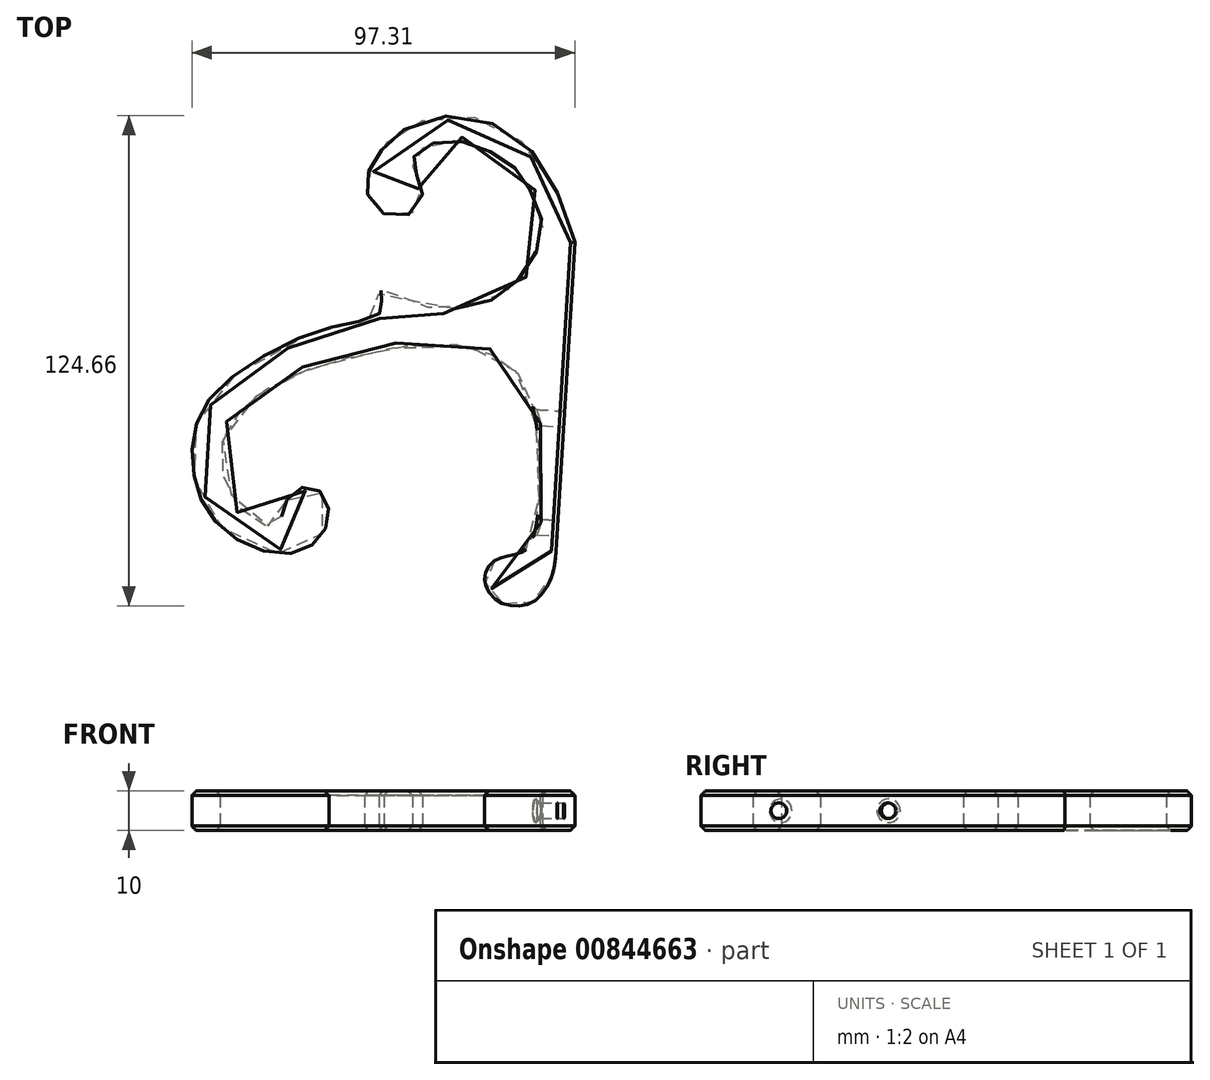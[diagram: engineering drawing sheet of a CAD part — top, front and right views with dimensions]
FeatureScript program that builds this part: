
annotation { "Feature Type Name" : "Feature", "Feature Type Description" : "" }
export const myFeature = defineFeature(function(context is Context, id is Id, definition is map)
    precondition{}
    {
        {
            var Q0;
            Q0=qCreatedBy(makeId("Top.planeOp"),FACE);
            var sketch = newSketch(context, id + "F0", { "sketchPlane" : qUnion([Q0])});
            skLineSegment(sketch, "E0", {"start": v(42, -44.18) * mm, "end": v(46.84, 34.44) * mm});
            skFitSpline(sketch, "E1", {"points": [v(46.84, 34.44) * mm, v(36.12, 57.16) * mm, v(16.47, 66.6) * mm, v(0.13, 60.73) * mm, v(-3.7, 55.37) * mm, v(-6.55, 49.76) * mm, v(-4.57, 44.53) * mm, v(0.03, 40.92) * mm, v(6.44, 42.64) * mm, v(8.06, 48.05) * mm, v(6.35, 52.02) * mm, v(5.63, 55.27) * mm, v(8.53, 58.54) * mm, v(16.08, 60.18) * mm, v(24.29, 57.88) * mm, v(31.84, 52.96) * mm, v(35.78, 47.05) * mm, v(38.57, 37.67) * mm, v(34.06, 26.93) * mm, v(26.02, 19.8) * mm, v(12.85, 17.45) * mm, v(3.55, 19.9) * mm, v(-0.96, 22.42) * mm, v(-2.23, 22.33) * mm, v(-2.95, 20.97) * mm, v(-1.68, 17.82) * mm, v(-5.79, 14.9) * mm, v(-18.56, 11.77) * mm, v(-40.39, 0) * mm, v(-49.26, -11.44) * mm, v(-50.24, -22.89) * mm, v(-46.9, -33.18) * mm, v(-37.7, -41.93) * mm, v(-25.15, -44.64) * mm, v(-17.84, -40.4) * mm, v(-15.67, -33.8) * mm, v(-18.56, -28.4) * mm, v(-24.07, -28.57) * mm, v(-27.4, -33.8) * mm, v(-28.58, -36.97) * mm, v(-34, -36.97) * mm, v(-40.7, -29.44) * mm, v(-43.14, -18.28) * mm, v(-38.31, -8.62) * mm, v(-30.17, -2.13) * mm, v(-15.4, 3.8) * mm, v(12.89, 8.63) * mm, v(26.1, 5.7) * mm, v(33.15, 0) * mm, v(37.09, -12.37) * mm, v(37.75, -31.08) * mm, v(35.32, -42.56) * mm, v(31.9, -44.82) * mm, v(25.93, -46.9) * mm, v(23.95, -51.95) * mm, v(28.19, -57.27) * mm, v(36.5, -56.82) * mm, v(41.1, -50.05) * mm, v(42, -44.18) * mm], "startDerivative": vector(-287.05, 889.88) * mm, "endDerivative": vector(28.23, 413.52) * mm});
            skSolve(sketch);
        }
        {
            var Q0;
            Q0=makeQuery(id+"F0.imprint","IMPRINT",FACE,{"disambiguationData":[TD([[makeQuery(id+"F0.imprint","IMPRINT",EDGE,{"derivedFrom":sQuery(id+"F0.wireOp",EDGE,"E0")}),1.0]])]});
            extrude(context, id + "F1", {"entities" : qUnion([Q0]), "depth" : 10 * mm, "offsetDistance" : 25 * mm});
        }
        {
            var Q0;
            Q0=makeQuery(id+"F1.opExtrude","CAP_EDGE",EDGE,{"disambiguationData":[OSD([sQuery(id+"F0.wireOp",EDGE,"E1")])],"isStart":false});
            var Q1;
            Q1=makeQuery(id+"F1.opExtrude","CAP_EDGE",EDGE,{"disambiguationData":[OSD([sQuery(id+"F0.wireOp",EDGE,"E0")])],"isStart":false});
            var Q2;
            Q2=makeQuery(id+"F1.opExtrude","CAP_EDGE",EDGE,{"disambiguationData":[OSD([sQuery(id+"F0.wireOp",EDGE,"E1")])],"isStart":true});
            var Q3;
            Q3=makeQuery(id+"F1.opExtrude","CAP_EDGE",EDGE,{"disambiguationData":[OSD([sQuery(id+"F0.wireOp",EDGE,"E0")])],"isStart":true});
            chamfer(context, id + "F2", {"entities" : qUnion([Q0, Q1, Q2, Q3]), "width" : 1.1 * mm, "tangentPropagation" : true});
        }
        {
            var Q0;
            Q0=makeQuery(id+"F1.opExtrude","SWEPT_FACE",FACE,{"disambiguationData":[OSD([sQuery(id+"F0.wireOp",EDGE,"E0")])]});
            var sketch = newSketch(context, id + "F3", { "sketchPlane" : qUnion([Q0])});
            skLineSegment(sketch, "E2", {"start": v(-41.51, 5) * mm, "end": v(37.26, 5) * mm, "construction": true});
            skCircle(sketch, "E3", {"center": v(-35.58, 5) * mm, "radius": 2 * mm});
            skCircle(sketch, "E4", {"center": v(-7.83, 5) * mm, "radius": 2 * mm});
            skPoint(sketch, "E5", {"position": v(-2.13, 5) * mm});
            skSolve(sketch);
        }
        {
            var Q0;
            Q0=makeQuery(id+"F3.imprint","IMPRINT",FACE,{"disambiguationData":[TD([[makeQuery(id+"F3.imprint","IMPRINT",EDGE,{"derivedFrom":sQuery(id+"F3.wireOp",EDGE,"E3")}),1.0]])]});
            var Q1;
            Q1=makeQuery(id+"F3.imprint","IMPRINT",FACE,{"disambiguationData":[TD([[makeQuery(id+"F3.imprint","IMPRINT",EDGE,{"derivedFrom":sQuery(id+"F3.wireOp",EDGE,"E4")}),1.0]])]});
            extrude(context, id + "F4", {"entities" : qUnion([Q0, Q1]), "operationType" : NewBodyOperationType.REMOVE, "oppositeDirection" : true, "depth" : 25 * mm, "offsetDistance" : 25 * mm});
        }
        {
            var Q0;
            Q0=makeQuery(id+"F4.boolean.opBoolean","INTERSECT",EDGE,{"derivedFrom":[makeQuery(id+"F1.opExtrude","SWEPT_FACE",FACE,{"disambiguationData":[OSD([sQuery(id+"F0.wireOp",EDGE,"E1")])]}),makeQuery(id+"F4.opExtrude","SWEPT_FACE",FACE,{"disambiguationData":[OSD([sQuery(id+"F3.wireOp",EDGE,"E3")])]})]});
            var Q1;
            Q1=makeQuery(id+"F4.boolean.opBoolean","INTERSECT",EDGE,{"derivedFrom":[makeQuery(id+"F1.opExtrude","SWEPT_FACE",FACE,{"disambiguationData":[OSD([sQuery(id+"F0.wireOp",EDGE,"E1")])]}),makeQuery(id+"F4.opExtrude","SWEPT_FACE",FACE,{"disambiguationData":[OSD([sQuery(id+"F3.wireOp",EDGE,"E4")])]})]});
            chamfer(context, id + "F5", {"entities" : qUnion([Q0, Q1]), "width" : 1 * mm, "tangentPropagation" : true});
        }
    });
